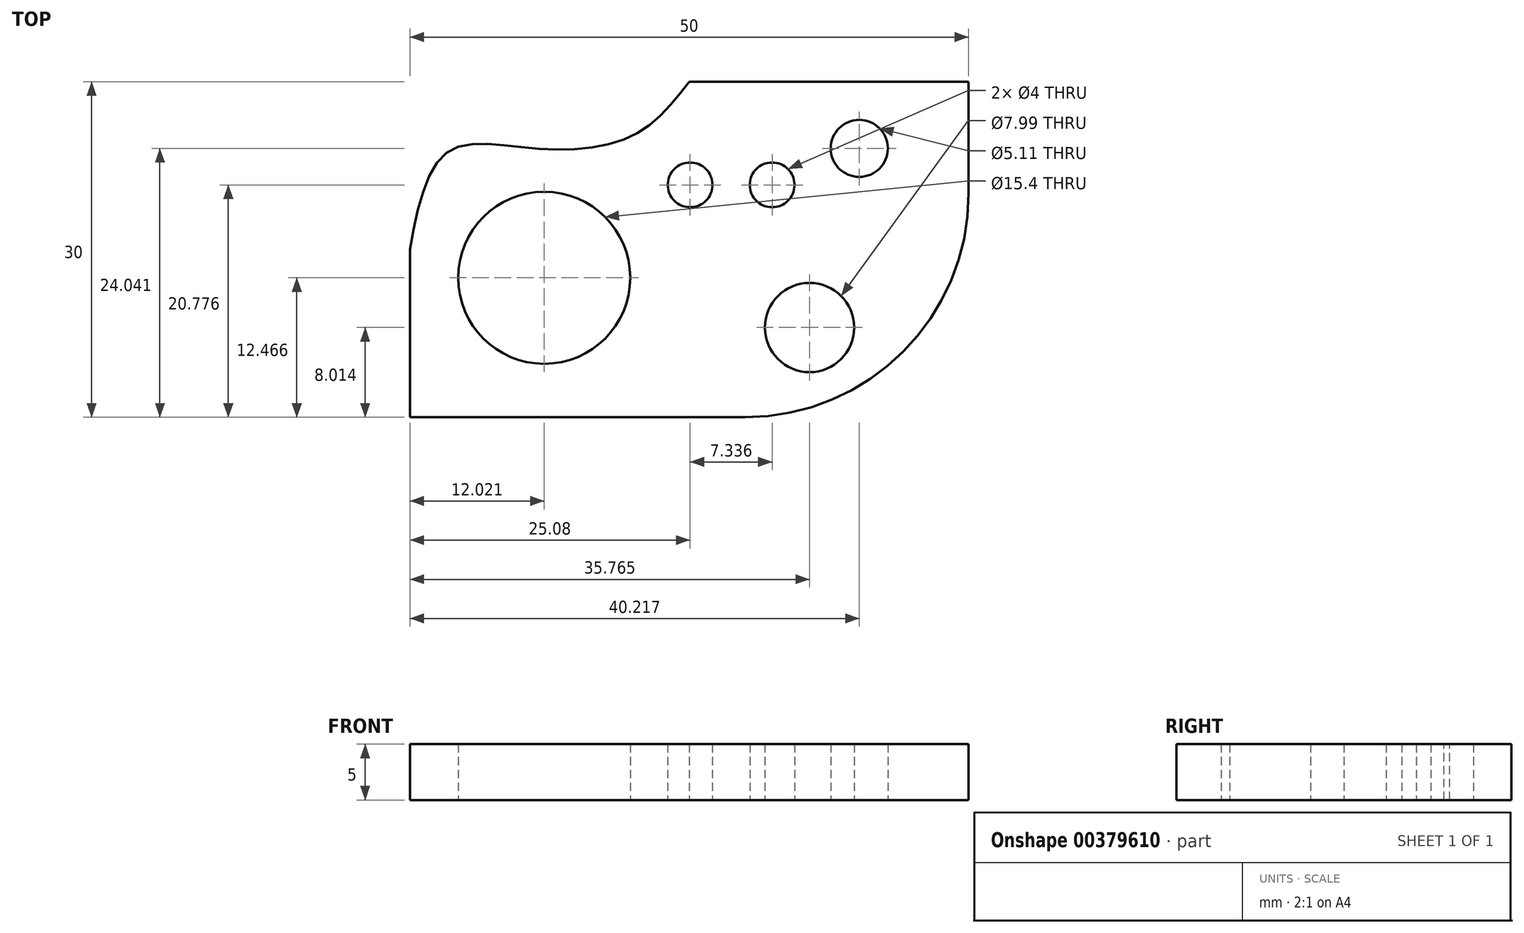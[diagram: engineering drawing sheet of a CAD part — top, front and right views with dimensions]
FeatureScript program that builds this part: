
annotation { "Feature Type Name" : "Feature", "Feature Type Description" : "" }
export const myFeature = defineFeature(function(context is Context, id is Id, definition is map)
    precondition{}
    {
        {
            var Q0;
            Q0=qCreatedBy(makeId("Top.planeOp"),FACE);
            var sketch = newSketch(context, id + "F0", { "sketchPlane" : qUnion([Q0])});
            skLineSegment(sketch, "E0.bottom", {"start": v(0, 0) * mm, "end": v(30, 0) * mm});
            skLineSegment(sketch, "E0.top", {"start": v(0, 30) * mm, "end": v(50, 30) * mm});
            skLineSegment(sketch, "E0.left", {"start": v(0, 0) * mm, "end": v(0, 30) * mm});
            skLineSegment(sketch, "E0.right", {"start": v(50, 20) * mm, "end": v(50, 30) * mm});
            skFitSpline(sketch, "E1", {"points": [v(0, 15) * mm, v(3.41, 23.74) * mm, v(11.13, 24.04) * mm, v(20.03, 25.23) * mm, v(25, 30) * mm], "startDerivative": vector(7.84, 41.44) * mm, "endDerivative": vector(18.74, 24.2) * mm});
            skPoint(sketch, "E2.visualSharp", {"position": v(50, 0) * mm});
            skArc(sketch, "E2.filletArc", {"start": v(30, 0) * mm, "mid": v(44.14, 5.86) * mm, "end": v(50, 20) * mm});
            skPoint(sketch, "E3", {"position": v(12.02, 12.47) * mm});
            skCircle(sketch, "E4", {"center": v(12.02, 12.47) * mm, "radius": 7.7 * mm});
            skCircle(sketch, "E5", {"center": v(40.22, 24.04) * mm, "radius": 2.55 * mm});
            skCircle(sketch, "E6", {"center": v(35.76, 8.01) * mm, "radius": 4 * mm});
            skCircle(sketch, "E7", {"center": v(25.08, 20.78) * mm, "radius": 2 * mm});
            skCircle(sketch, "E8", {"center": v(32.42, 20.78) * mm, "radius": 2 * mm});
            skSolve(sketch);
        }
        {
            var Q0;
            {var subQ1=sQuery(id+"F0.wireOp",EDGE,"E0.bottom");Q0=makeQuery(id+"F0.imprint","IMPRINT",FACE,{"disambiguationData":[TD([[makeQuery(id+"F0.imprint","IMPRINT",EDGE,{"derivedFrom":subQ1}),1.0]])]});}
            extrude(context, id + "F1", {"entities" : qUnion([Q0]), "depth" : 5 * mm});
        }
    });
